# Revit family: Kugelhahn mit Hebelgriff und Rückflussverhinderer 2110
name_source: partatom
category: Rohrzubehör
revit_build: Autodesk Revit 2018 (Build: 20190510_1515(x64)
units: mm (PartAtom-declared; Revit-internal decimal feet)

## family parameters
Arbeitsebenenbasiert = Nein
Beim Laden mit Abzugskörper schneiden = Nein
Bemaßung runder Anschluss = Durchmesser verwenden
Gemeinsam genutzt = Nein
Immer vertikal = Ja
OmniClass-Nummer = 23.65.55.14
OmniClass-Titel = Valves for Liquid Services
Teiletyp = Unterbricht

## types (1)
- Kugelhahn mit Hebelgriff und Rückflussverhinderer 2110
    Anwendungsgebiet = Der HERZ Kugelhahn mit Hebelgriff und Rückflussverhinderer wird in Trinkwassersystemen verwendet und dient als Absperreinrichtung.
Generell werden Kugelhähne überall dort eingesetzt, wo der Durchfluss verlässlich unterbrochen werden muss.
Der Rückflussverhinderer stellt sicher, dass ein Medienstrom ausschließlich in Durchflussrichtung stattfindet.
    Gehäuse = geschmiedetes entzinkungsbeständiges Messing nach EN 12165, CW626N
    Gehäuse Rückflussverhinderer = POM
    Gewinde = nach ISO 228
    Handgriff = Hebelgriff, grün, Stahlblech - verzinkt
    Hersteller = HERZ Armaturen Ges.m.b.H.
    Hinweis = Gemäß Art 33 der REACH-Verordnung (EG Nr. 1907/2006) sind wir verpflichtet, darauf hinzuweisen, dass der Stoff Blei auf der SVHC-Liste geführt wird und dass alle aus Messing bestehenden Bauteile, die in unseren Erzeugnissen verarbeitet sind, mehr als 0,1 % (w/w) Blei (CAS: 7439-92-1 / EINECS: 231-100-4) enthalten.
Da Blei als Legierungsbestandteil fest gebunden ist, sind keine Expositionen zu erwarten und daher sind keine zusätzlichen Angaben zur sicheren Verwendung notwendig.
    Kugel = geschmiedetes entzinkungsbeständiges Messing nach EN 12165, volle Bohrung, verchromt, CW626N
    Kugeldichtung = PTFE
    L03 = 5 mm  [stored 0.0164042 ft]
    Max. Betriebsdruck = 2500000.0 Pa
    Max. Betriebstemperatur = 85 °C
    Medium = Trinkwasser
    Min. Betriebstemperatur = -10 °C
    Min. Betriebstemperatur (Wasser) = 1 °C
    O-Ring Rückflussverhinderer = Silikon
    R01 = 7 mm  [stored 0.0229659 ft]
    S04 = 5 mm  [stored 0.0164042 ft]
    SCTWCODE = 04;04;02
    SCTWSEQ = FW;SBT_TYP_FW="102";2
    SC_NennweiteBerechnet = 0
    Spindel = Messing nach EN 12164, CW614N
    Spindeldichtung = EPDM
    URL = www.herz-armaturen.at
    W01 = 45.00°

note: [stored X ft] marks values corroborated as IEEE doubles in the binary element streams (Revit-internal decimal feet)
